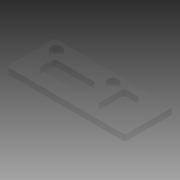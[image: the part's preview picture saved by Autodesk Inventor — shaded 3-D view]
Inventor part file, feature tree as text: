
AUTODESK INVENTOR PART (.ipt)
format: ipt  version: 2015 (Build 190159000, 159)  size: 123,392 bytes
history: native  units: mm
features: extrude x1, fillet x1, hole x1, reference x1
ambient origin geometry x8: Origin, YZ Plane, XZ Plane, XY Plane, X Axis, Y Axis, Z Axis, Center Point
bodies: Solid1 (feature_tree)
feature tree (4):
  extrude  "Extrusión1"  Depth=1.0mm
  fillet  "Empalme1"  Radius=1.0mm
  hole  "Agujero1"  [1 undecoded]
  reference  "Referencia1"
note: 1 required parameter value undecoded (feature->parameter linkage not recoverable at this tier; creation-order binding heuristic only, values carry confidence <= 0.55)
